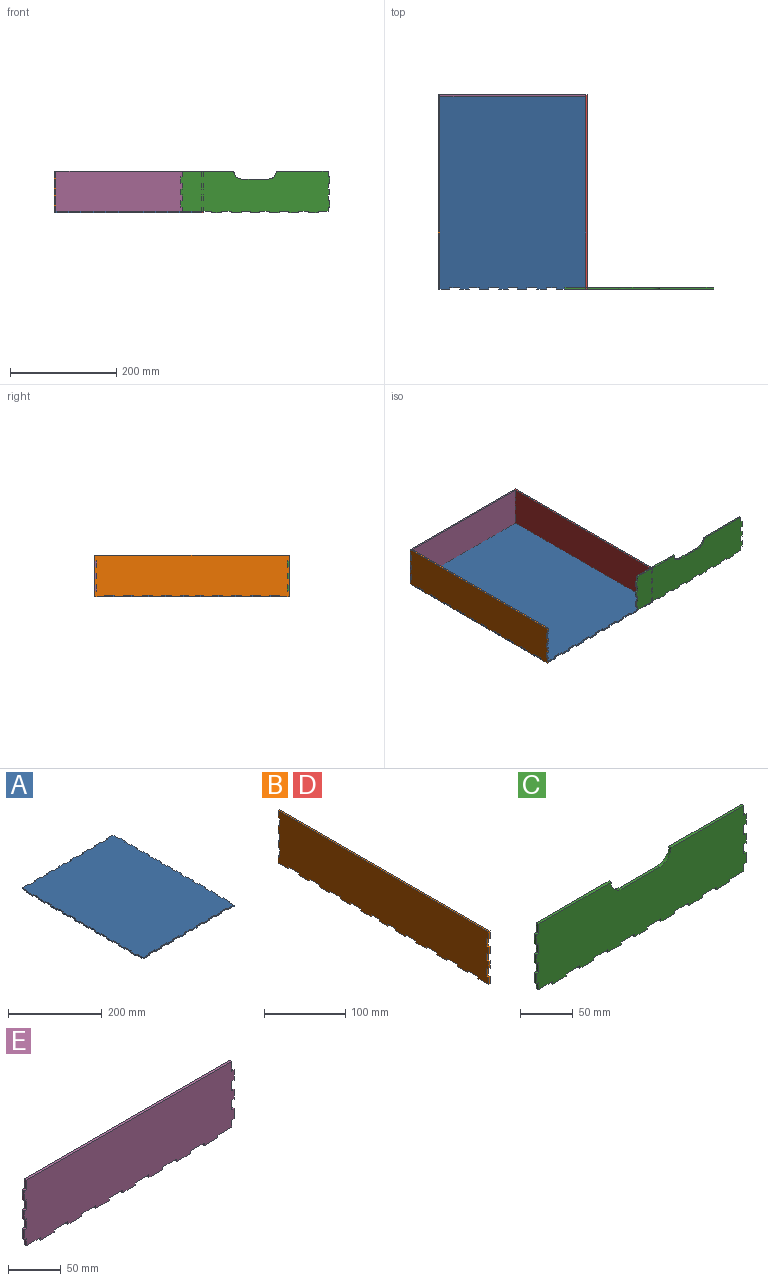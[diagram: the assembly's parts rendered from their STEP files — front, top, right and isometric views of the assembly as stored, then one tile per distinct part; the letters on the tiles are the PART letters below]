
ASSEMBLY  parts=5 mates=4
PART A: 142 faces, bbox 281x366x3 mm
  f0: plane 18x3mm, normal (-1,0,0), area 54mm2, adj f1,f139,f140,f141
  f1: plane 3x3mm, normal (0,1,0), area 9mm2, adj f0,f2,f140,f141
  f2: plane 18x3mm, normal (-1,0,0), area 54mm2, adj f1,f3,f140,f141
  f3: plane 3x3mm, normal (0,-1,0), area 9mm2, adj f2,f4,f140,f141
  f4: plane 18x3mm, normal (-1,0,0), area 54mm2, adj f3,f5,f140,f141
  f5: plane 3x3mm, normal (0,1,0), area 9mm2, adj f4,f6,f140,f141
  f6: plane 18x3mm, normal (-1,0,0), area 54mm2, adj f5,f7,f140,f141
  f7: plane 3x3mm, normal (0,-1,0), area 9mm2, adj f6,f8,f140,f141
  f8: plane 18x3mm, normal (-1,0,0), area 54mm2, adj f7,f9,f140,f141
  f9: plane 3x3mm, normal (0,1,0), area 9mm2, adj f8,f10,f140,f141
  f10: plane 18x3mm, normal (-1,0,0), area 54mm2, adj f9,f11,f140,f141
  f11: plane 3x3mm, normal (0,-1,0), area 9mm2, adj f10,f12,f140,f141
  f12: plane 18x3mm, normal (-1,0,0), area 54mm2, adj f11,f13,f140,f141
  f13: plane 3x3mm, normal (0,1,0), area 9mm2, adj f12,f14,f140,f141
  f14: plane 18x3mm, normal (-1,0,0), area 54mm2, adj f13,f15,f140,f141
  f15: plane 3x3mm, normal (0,-1,0), area 9mm2, adj f14,f16,f140,f141
  f16: plane 18x3mm, normal (-1,0,0), area 54mm2, adj f15,f17,f140,f141
  f17: plane 3x3mm, normal (0,1,0), area 9mm2, adj f16,f18,f140,f141
  f18: plane 14x3mm, normal (-1,0,0), area 42mm2, adj f17,f19,f140,f141
  f19: plane 3x3mm, normal (0,-1,0), area 9mm2, adj f18,f20,f140,f141
  f20: plane 14x3mm, normal (-1,0,0), area 42mm2, adj f19,f21,f140,f141
  f21: plane 3x3mm, normal (0,1,0), area 9mm2, adj f20,f22,f140,f141
  f22: plane 14x3mm, normal (-1,0,0), area 42mm2, adj f21,f23,f140,f141
  f23: plane 3x3mm, normal (0,-1,0), area 9mm2, adj f22,f24,f140,f141
  f24: plane 18x3mm, normal (-1,0,0), area 54mm2, adj f23,f25,f140,f141
  f25: plane 3x3mm, normal (0,1,0), area 9mm2, adj f24,f26,f140,f141
  f26: plane 18x3mm, normal (-1,0,0), area 54mm2, adj f25,f27,f140,f141
  f27: plane 3x3mm, normal (0,-1,0), area 9mm2, adj f26,f28,f140,f141
  f28: plane 18x3mm, normal (-1,0,0), area 54mm2, adj f27,f29,f140,f141
  f29: plane 3x3mm, normal (0,1,0), area 9mm2, adj f28,f30,f140,f141
  f30: plane 18x3mm, normal (-1,0,0), area 54mm2, adj f29,f31,f140,f141
  f31: plane 3x3mm, normal (0,-1,0), area 9mm2, adj f30,f32,f140,f141
  f32: plane 18x3mm, normal (-1,0,0), area 54mm2, adj f31,f33,f140,f141
  f33: plane 3x3mm, normal (0,1,0), area 9mm2, adj f32,f34,f140,f141
  f34: plane 18x3mm, normal (-1,0,0), area 54mm2, adj f33,f35,f140,f141
  f35: plane 3x3mm, normal (0,-1,0), area 9mm2, adj f34,f36,f140,f141
  f36: plane 18x3mm, normal (-1,0,0), area 54mm2, adj f35,f37,f140,f141
  f37: plane 3x3mm, normal (0,1,0), area 9mm2, adj f36,f38,f140,f141
  f38: plane 18x3mm, normal (-1,0,0), area 54mm2, adj f37,f39,f140,f141
  f39: plane 3x3mm, normal (0,-1,0), area 9mm2, adj f38,f40,f140,f141
  f40: plane 18x3mm, normal (-1,0,0), area 54mm2, adj f39,f41,f140,f141
  f41: plane 18.5x3mm, normal (0,-1,0), area 55.5mm2, adj f40,f42,f140,f141
  f42: plane 3x3mm, normal (1,0,0), area 9mm2, adj f41,f43,f140,f141
  f43: plane 18.5x3mm, normal (0,-1,0), area 55.5mm2, adj f42,f44,f140,f141
  f44: plane 3x3mm, normal (-1,0,0), area 9mm2, adj f43,f45,f140,f141
  f45: plane 18.5x3mm, normal (0,-1,0), area 55.5mm2, adj f44,f46,f140,f141
  f46: plane 3x3mm, normal (1,0,0), area 9mm2, adj f45,f47,f140,f141
  f47: plane 18.5x3mm, normal (0,-1,0), area 55.5mm2, adj f46,f48,f140,f141
  f48: plane 3x3mm, normal (-1,0,0), area 9mm2, adj f47,f49,f140,f141
  f49: plane 18.5x3mm, normal (0,-1,0), area 55.5mm2, adj f48,f50,f140,f141
  f50: plane 3x3mm, normal (1,0,0), area 9mm2, adj f49,f51,f140,f141
  f51: plane 18.5x3mm, normal (0,-1,0), area 55.5mm2, adj f50,f52,f140,f141
  f52: plane 3x3mm, normal (-1,0,0), area 9mm2, adj f51,f53,f140,f141
  f53: plane 18x3mm, normal (0,-1,0), area 54mm2, adj f52,f54,f140,f141
  f54: plane 3x3mm, normal (1,0,0), area 9mm2, adj f53,f55,f140,f141
  f55: plane 17x3mm, normal (0,-1,0), area 51mm2, adj f54,f56,f140,f141
  f56: plane 3x3mm, normal (-1,0,0), area 9mm2, adj f55,f57,f140,f141
  f57: plane 18x3mm, normal (0,-1,0), area 54mm2, adj f56,f58,f140,f141
  f58: plane 3x3mm, normal (1,0,0), area 9mm2, adj f57,f59,f140,f141
  f59: plane 18.5x3mm, normal (0,-1,0), area 55.5mm2, adj f58,f60,f140,f141
  f60: plane 3x3mm, normal (-1,0,0), area 9mm2, adj f59,f61,f140,f141
  f61: plane 18.5x3mm, normal (0,-1,0), area 55.5mm2, adj f60,f62,f140,f141
  f62: plane 3x3mm, normal (1,0,0), area 9mm2, adj f61,f63,f140,f141
  f63: plane 18.5x3mm, normal (0,-1,0), area 55.5mm2, adj f62,f64,f140,f141
  f64: plane 3x3mm, normal (-1,0,0), area 9mm2, adj f63,f65,f140,f141
  f65: plane 18.5x3mm, normal (0,-1,0), area 55.5mm2, adj f64,f66,f140,f141
  f66: plane 3x3mm, normal (1,0,0), area 9mm2, adj f65,f67,f140,f141
  f67: plane 18.5x3mm, normal (0,-1,0), area 55.5mm2, adj f66,f68,f140,f141
  f68: plane 3x3mm, normal (-1,0,0), area 9mm2, adj f67,f69,f140,f141
  f69: plane 18.5x3mm, normal (0,-1,0), area 55.5mm2, adj f68,f70,f140,f141
  f70: plane 18x3mm, normal (1,0,0), area 54mm2, adj f69,f71,f140,f141
  f71: plane 3x3mm, normal (0,-1,0), area 9mm2, adj f70,f72,f140,f141
  f72: plane 18x3mm, normal (1,0,0), area 54mm2, adj f71,f73,f140,f141
  f73: plane 3x3mm, normal (0,1,0), area 9mm2, adj f72,f74,f140,f141
  f74: plane 18x3mm, normal (1,0,0), area 54mm2, adj f73,f75,f140,f141
  f75: plane 3x3mm, normal (0,-1,0), area 9mm2, adj f74,f76,f140,f141
  f76: plane 18x3mm, normal (1,0,0), area 54mm2, adj f75,f77,f140,f141
  f77: plane 3x3mm, normal (0,1,0), area 9mm2, adj f76,f78,f140,f141
  f78: plane 18x3mm, normal (1,0,0), area 54mm2, adj f77,f79,f140,f141
  f79: plane 3x3mm, normal (0,-1,0), area 9mm2, adj f78,f80,f140,f141
  f80: plane 18x3mm, normal (1,0,0), area 54mm2, adj f79,f81,f140,f141
  f81: plane 3x3mm, normal (0,1,0), area 9mm2, adj f80,f82,f140,f141
  f82: plane 18x3mm, normal (1,0,0), area 54mm2, adj f81,f83,f140,f141
  f83: plane 3x3mm, normal (0,-1,0), area 9mm2, adj f82,f84,f140,f141
  f84: plane 18x3mm, normal (1,0,0), area 54mm2, adj f83,f85,f140,f141
  f85: plane 3x3mm, normal (0,1,0), area 9mm2, adj f84,f86,f140,f141
  f86: plane 18x3mm, normal (1,0,0), area 54mm2, adj f85,f87,f140,f141
  f87: plane 3x3mm, normal (0,-1,0), area 9mm2, adj f86,f88,f140,f141
  f88: plane 14x3mm, normal (1,0,0), area 42mm2, adj f87,f89,f140,f141
  f89: plane 3x3mm, normal (0,1,0), area 9mm2, adj f88,f90,f140,f141
  f90: plane 14x3mm, normal (1,0,0), area 42mm2, adj f89,f91,f140,f141
  f91: plane 3x3mm, normal (0,-1,0), area 9mm2, adj f90,f92,f140,f141
  f92: plane 14x3mm, normal (1,0,0), area 42mm2, adj f91,f93,f140,f141
  f93: plane 3x3mm, normal (0,1,0), area 9mm2, adj f92,f94,f140,f141
  f94: plane 18x3mm, normal (1,0,0), area 54mm2, adj f93,f95,f140,f141
  f95: plane 3x3mm, normal (0,-1,0), area 9mm2, adj f94,f96,f140,f141
  f96: plane 18x3mm, normal (1,0,0), area 54mm2, adj f95,f97,f140,f141
  f97: plane 3x3mm, normal (0,1,0), area 9mm2, adj f96,f98,f140,f141
  f98: plane 18x3mm, normal (1,0,0), area 54mm2, adj f97,f99,f140,f141
  f99: plane 3x3mm, normal (0,-1,0), area 9mm2, adj f98,f100,f140,f141
  f100: plane 18x3mm, normal (1,0,0), area 54mm2, adj f99,f101,f140,f141
  f101: plane 3x3mm, normal (0,1,0), area 9mm2, adj f100,f102,f140,f141
  f102: plane 18x3mm, normal (1,0,0), area 54mm2, adj f101,f103,f140,f141
  f103: plane 3x3mm, normal (0,-1,0), area 9mm2, adj f102,f104,f140,f141
  f104: plane 18x3mm, normal (1,0,0), area 54mm2, adj f103,f105,f140,f141
  f105: plane 3x3mm, normal (0,1,0), area 9mm2, adj f104,f106,f140,f141
  f106: plane 18x3mm, normal (1,0,0), area 54mm2, adj f105,f107,f140,f141
  f107: plane 3x3mm, normal (0,-1,0), area 9mm2, adj f106,f108,f140,f141
  f108: plane 18x3mm, normal (1,0,0), area 54mm2, adj f107,f109,f140,f141
  f109: plane 3x3mm, normal (0,1,0), area 9mm2, adj f108,f110,f140,f141
  f110: plane 18x3mm, normal (1,0,0), area 54mm2, adj f109,f111,f140,f141
  f111: plane 18.5x3mm, normal (0,1,0), area 55.5mm2, adj f110,f112,f140,f141
  f112: plane 3x3mm, normal (-1,0,0), area 9mm2, adj f111,f113,f140,f141
  f113: plane 18.5x3mm, normal (0,1,0), area 55.5mm2, adj f112,f114,f140,f141
  f114: plane 3x3mm, normal (1,0,0), area 9mm2, adj f113,f115,f140,f141
  f115: plane 18.5x3mm, normal (0,1,0), area 55.5mm2, adj f114,f116,f140,f141
  f116: plane 3x3mm, normal (-1,0,0), area 9mm2, adj f115,f117,f140,f141
  f117: plane 18.5x3mm, normal (0,1,0), area 55.5mm2, adj f116,f118,f140,f141
  f118: plane 3x3mm, normal (1,0,0), area 9mm2, adj f117,f119,f140,f141
  f119: plane 18.5x3mm, normal (0,1,0), area 55.5mm2, adj f118,f120,f140,f141
  f120: plane 3x3mm, normal (-1,0,0), area 9mm2, adj f119,f121,f140,f141
  f121: plane 18.5x3mm, normal (0,1,0), area 55.5mm2, adj f120,f122,f140,f141
  f122: plane 3x3mm, normal (1,0,0), area 9mm2, adj f121,f123,f140,f141
  f123: plane 18x3mm, normal (0,1,0), area 54mm2, adj f122,f124,f140,f141
  f124: plane 3x3mm, normal (-1,0,0), area 9mm2, adj f123,f125,f140,f141
  f125: plane 17x3mm, normal (0,1,0), area 51mm2, adj f124,f126,f140,f141
  f126: plane 3x3mm, normal (1,0,0), area 9mm2, adj f125,f127,f140,f141
  f127: plane 18x3mm, normal (0,1,0), area 54mm2, adj f126,f128,f140,f141
  f128: plane 3x3mm, normal (-1,0,0), area 9mm2, adj f127,f129,f140,f141
  f129: plane 18.5x3mm, normal (0,1,0), area 55.5mm2, adj f128,f130,f140,f141
  f130: plane 3x3mm, normal (1,0,0), area 9mm2, adj f129,f131,f140,f141
  f131: plane 18.5x3mm, normal (0,1,0), area 55.5mm2, adj f130,f132,f140,f141
  f132: plane 3x3mm, normal (-1,0,0), area 9mm2, adj f131,f133,f140,f141
  f133: plane 18.5x3mm, normal (0,1,0), area 55.5mm2, adj f132,f134,f140,f141
  f134: plane 3x3mm, normal (1,0,0), area 9mm2, adj f133,f135,f140,f141
  f135: plane 18.5x3mm, normal (0,1,0), area 55.5mm2, adj f134,f136,f140,f141
  f136: plane 3x3mm, normal (-1,0,0), area 9mm2, adj f135,f137,f140,f141
  f137: plane 18.5x3mm, normal (0,1,0), area 55.5mm2, adj f136,f138,f140,f141
  f138: plane 3x3mm, normal (1,0,0), area 9mm2, adj f137,f139,f140,f141
  f139: plane 18.5x3mm, normal (0,1,0), area 55.5mm2, adj f0,f138,f140,f141
  f140: plane 366x281mm, normal (0,0,1), area 100914mm2, adj f0,f1,f2,f3,f4,f5,f6,f7
  f141: plane 366x281mm, normal (0,0,-1), area 100914mm2, adj f0,f1,f2,f3,f4,f5,f6,f7
PART B: 70 faces, bbox 3x366x79 mm
  f0: plane 3x3mm, normal (0,-1,0), area 9mm2, adj f1,f67,f68,f69
  f1: plane 18x3mm, normal (0,0,-1), area 54mm2, adj f0,f2,f68,f69
  f2: plane 3x3mm, normal (0,1,0), area 9mm2, adj f1,f3,f68,f69
  f3: plane 18x3mm, normal (0,0,-1), area 54mm2, adj f2,f4,f68,f69
  f4: plane 3x3mm, normal (0,-1,0), area 9mm2, adj f3,f5,f68,f69
  f5: plane 18x3mm, normal (0,0,-1), area 54mm2, adj f4,f6,f68,f69
  f6: plane 3x3mm, normal (0,1,0), area 9mm2, adj f5,f7,f68,f69
  f7: plane 18x3mm, normal (0,0,-1), area 54mm2, adj f6,f8,f68,f69
  f8: plane 3x3mm, normal (0,-1,0), area 9mm2, adj f7,f9,f68,f69
  f9: plane 18x3mm, normal (0,0,-1), area 54mm2, adj f8,f10,f68,f69
  f10: plane 3x3mm, normal (0,1,0), area 9mm2, adj f9,f11,f68,f69
  f11: plane 14x3mm, normal (0,0,-1), area 42mm2, adj f10,f12,f68,f69
  f12: plane 3x3mm, normal (0,-1,0), area 9mm2, adj f11,f13,f68,f69
  f13: plane 14x3mm, normal (0,0,-1), area 42mm2, adj f12,f14,f68,f69
  f14: plane 3x3mm, normal (0,1,0), area 9mm2, adj f13,f15,f68,f69
  f15: plane 14x3mm, normal (0,0,-1), area 42mm2, adj f14,f16,f68,f69
  f16: plane 3x3mm, normal (0,-1,0), area 9mm2, adj f15,f17,f68,f69
  f17: plane 18x3mm, normal (0,0,-1), area 54mm2, adj f16,f18,f68,f69
  f18: plane 3x3mm, normal (0,1,0), area 9mm2, adj f17,f19,f68,f69
  f19: plane 18x3mm, normal (0,0,-1), area 54mm2, adj f18,f20,f68,f69
  f20: plane 3x3mm, normal (0,-1,0), area 9mm2, adj f19,f21,f68,f69
  f21: plane 18x3mm, normal (0,0,-1), area 54mm2, adj f20,f22,f68,f69
  f22: plane 3x3mm, normal (0,1,0), area 9mm2, adj f21,f23,f68,f69
  f23: plane 18x3mm, normal (0,0,-1), area 54mm2, adj f22,f24,f68,f69
  f24: plane 3x3mm, normal (0,-1,0), area 9mm2, adj f23,f25,f68,f69
  f25: plane 18x3mm, normal (0,0,-1), area 54mm2, adj f24,f26,f68,f69
  f26: plane 3x3mm, normal (0,1,0), area 9mm2, adj f25,f27,f68,f69
  f27: plane 18x3mm, normal (0,0,-1), area 54mm2, adj f26,f28,f68,f69
  f28: plane 3x3mm, normal (0,-1,0), area 9mm2, adj f27,f29,f68,f69
  f29: plane 18x3mm, normal (0,0,-1), area 54mm2, adj f28,f30,f68,f69
  f30: plane 3x3mm, normal (0,1,0), area 9mm2, adj f29,f31,f68,f69
  f31: plane 18x3mm, normal (0,0,-1), area 54mm2, adj f30,f32,f68,f69
  f32: plane 3x3mm, normal (0,-1,0), area 9mm2, adj f31,f33,f68,f69
  f33: plane 18x3mm, normal (0,0,-1), area 54mm2, adj f32,f34,f68,f69
  f34: plane 11x3mm, normal (0,1,0), area 33mm2, adj f33,f35,f68,f69
  f35: plane 3x3mm, normal (0,0,1), area 9mm2, adj f34,f36,f68,f69
  f36: plane 12x3mm, normal (0,1,0), area 36mm2, adj f35,f37,f68,f69
  f37: plane 3x3mm, normal (0,0,-1), area 9mm2, adj f36,f38,f68,f69
  f38: plane 11x3mm, normal (0,1,0), area 33mm2, adj f37,f39,f68,f69
  f39: plane 3x3mm, normal (0,0,1), area 9mm2, adj f38,f40,f68,f69
  f40: plane 11x3mm, normal (0,1,0), area 33mm2, adj f39,f41,f68,f69
  f41: plane 3x3mm, normal (0,0,-1), area 9mm2, adj f40,f42,f68,f69
  f42: plane 11x3mm, normal (0,1,0), area 33mm2, adj f41,f43,f68,f69
  f43: plane 3x3mm, normal (0,0,1), area 9mm2, adj f42,f44,f68,f69
  f44: plane 12x3mm, normal (0,1,0), area 36mm2, adj f43,f45,f68,f69
  f45: plane 3x3mm, normal (0,0,-1), area 9mm2, adj f44,f46,f68,f69
  f46: plane 11x3mm, normal (0,1,0), area 33mm2, adj f45,f47,f68,f69
  f47: plane 366x3mm, normal (0,0,1), area 1098mm2, adj f46,f48,f68,f69
  f48: plane 11x3mm, normal (0,-1,0), area 33mm2, adj f47,f49,f68,f69
  f49: plane 3x3mm, normal (0,0,-1), area 9mm2, adj f48,f50,f68,f69
  f50: plane 12x3mm, normal (0,-1,0), area 36mm2, adj f49,f51,f68,f69
  f51: plane 3x3mm, normal (0,0,1), area 9mm2, adj f50,f52,f68,f69
  f52: plane 11x3mm, normal (0,-1,0), area 33mm2, adj f51,f53,f68,f69
  f53: plane 3x3mm, normal (0,0,-1), area 9mm2, adj f52,f54,f68,f69
  f54: plane 11x3mm, normal (0,-1,0), area 33mm2, adj f53,f55,f68,f69
  f55: plane 3x3mm, normal (0,0,1), area 9mm2, adj f54,f56,f68,f69
  f56: plane 11x3mm, normal (0,-1,0), area 33mm2, adj f55,f57,f68,f69
  f57: plane 3x3mm, normal (0,0,-1), area 9mm2, adj f56,f58,f68,f69
  f58: plane 12x3mm, normal (0,-1,0), area 36mm2, adj f57,f59,f68,f69
  f59: plane 3x3mm, normal (0,0,1), area 9mm2, adj f58,f60,f68,f69
  f60: plane 11x3mm, normal (0,-1,0), area 33mm2, adj f59,f61,f68,f69
  f61: plane 18x3mm, normal (0,0,-1), area 54mm2, adj f60,f62,f68,f69
  f62: plane 3x3mm, normal (0,1,0), area 9mm2, adj f61,f63,f68,f69
  f63: plane 18x3mm, normal (0,0,-1), area 54mm2, adj f62,f64,f68,f69
  f64: plane 3x3mm, normal (0,-1,0), area 9mm2, adj f63,f65,f68,f69
  f65: plane 18x3mm, normal (0,0,-1), area 54mm2, adj f64,f66,f68,f69
  f66: plane 3x3mm, normal (0,1,0), area 9mm2, adj f65,f67,f68,f69
  f67: plane 18x3mm, normal (0,0,-1), area 54mm2, adj f0,f66,f68,f69
  f68: plane 366x79mm, normal (1,0,0), area 28188mm2, adj f0,f1,f2,f3,f4,f5,f6,f7
  f69: plane 366x79mm, normal (-1,0,0), area 28188mm2, adj f0,f1,f2,f3,f4,f5,f6,f7
PART C: 62 faces, bbox 281x3x79 mm
  f0: plane 3x3mm, normal (0,0,-1), area 9mm2, adj f1,f59,f60,f61
  f1: plane 11x3mm, normal (1,0,0), area 33mm2, adj f0,f2,f60,f61
  f2: plane 3x3mm, normal (0,0,1), area 9mm2, adj f1,f3,f60,f61
  f3: plane 11x3mm, normal (1,0,0), area 33mm2, adj f2,f4,f60,f61
  f4: plane 3x3mm, normal (0,0,-1), area 9mm2, adj f3,f5,f60,f61
  f5: plane 12x3mm, normal (1,0,0), area 36mm2, adj f4,f6,f60,f61
  f6: plane 3x3mm, normal (0,0,1), area 9mm2, adj f5,f7,f60,f61
  f7: plane 11x3mm, normal (1,0,0), area 33mm2, adj f6,f8,f60,f61
  f8: plane 97.5x3mm, normal (0,0,1), area 292.5mm2, adj f7,f9,f60,f61
  f9: cylinder r=15mm len=15mm, axis (0,-1,0), area 70.7mm2, adj f8,f10,f60,f61
  f10: plane 50x3mm, normal (0,0,1), area 150mm2, adj f9,f11,f60,f61
  f11: cylinder r=15mm len=15mm, axis (0,-1,0), area 70.7mm2, adj f10,f12,f60,f61
  f12: plane 97.5x3mm, normal (0,0,1), area 292.5mm2, adj f11,f13,f60,f61
  f13: plane 11x3mm, normal (-1,0,0), area 33mm2, adj f12,f14,f60,f61
  f14: plane 3x3mm, normal (0,0,1), area 9mm2, adj f13,f15,f60,f61
  f15: plane 12x3mm, normal (-1,0,0), area 36mm2, adj f14,f16,f60,f61
  f16: plane 3x3mm, normal (0,0,-1), area 9mm2, adj f15,f17,f60,f61
  f17: plane 11x3mm, normal (-1,0,0), area 33mm2, adj f16,f18,f60,f61
  f18: plane 3x3mm, normal (0,0,1), area 9mm2, adj f17,f19,f60,f61
  f19: plane 11x3mm, normal (-1,0,0), area 33mm2, adj f18,f20,f60,f61
  f20: plane 3x3mm, normal (0,0,-1), area 9mm2, adj f19,f21,f60,f61
  f21: plane 11x3mm, normal (-1,0,0), area 33mm2, adj f20,f22,f60,f61
  f22: plane 3x3mm, normal (0,0,1), area 9mm2, adj f21,f23,f60,f61
  f23: plane 12x3mm, normal (-1,0,0), area 36mm2, adj f22,f24,f60,f61
  f24: plane 3x3mm, normal (0,0,-1), area 9mm2, adj f23,f25,f60,f61
  f25: plane 8x3mm, normal (-1,0,0), area 24mm2, adj f24,f26,f60,f61
  f26: plane 18.5x3mm, normal (0,0,-1), area 55.5mm2, adj f25,f27,f60,f61
  f27: plane 3x3mm, normal (-1,0,0), area 9mm2, adj f26,f28,f60,f61
  f28: plane 18.5x3mm, normal (0,0,-1), area 55.5mm2, adj f27,f29,f60,f61
  f29: plane 3x3mm, normal (1,0,0), area 9mm2, adj f28,f30,f60,f61
  f30: plane 18.5x3mm, normal (0,0,-1), area 55.5mm2, adj f29,f31,f60,f61
  f31: plane 3x3mm, normal (-1,0,0), area 9mm2, adj f30,f32,f60,f61
  f32: plane 18.5x3mm, normal (0,0,-1), area 55.5mm2, adj f31,f33,f60,f61
  f33: plane 3x3mm, normal (1,0,0), area 9mm2, adj f32,f34,f60,f61
  f34: plane 18.5x3mm, normal (0,0,-1), area 55.5mm2, adj f33,f35,f60,f61
  f35: plane 3x3mm, normal (-1,0,0), area 9mm2, adj f34,f36,f60,f61
  f36: plane 18.5x3mm, normal (0,0,-1), area 55.5mm2, adj f35,f37,f60,f61
  f37: plane 3x3mm, normal (1,0,0), area 9mm2, adj f36,f38,f60,f61
  f38: plane 18x3mm, normal (0,0,-1), area 54mm2, adj f37,f39,f60,f61
  f39: plane 3x3mm, normal (-1,0,0), area 9mm2, adj f38,f40,f60,f61
  f40: plane 17x3mm, normal (0,0,-1), area 51mm2, adj f39,f41,f60,f61
  f41: plane 3x3mm, normal (1,0,0), area 9mm2, adj f40,f42,f60,f61
  f42: plane 18x3mm, normal (0,0,-1), area 54mm2, adj f41,f43,f60,f61
  f43: plane 3x3mm, normal (-1,0,0), area 9mm2, adj f42,f44,f60,f61
  f44: plane 18.5x3mm, normal (0,0,-1), area 55.5mm2, adj f43,f45,f60,f61
  f45: plane 3x3mm, normal (1,0,0), area 9mm2, adj f44,f46,f60,f61
  f46: plane 18.5x3mm, normal (0,0,-1), area 55.5mm2, adj f45,f47,f60,f61
  f47: plane 3x3mm, normal (-1,0,0), area 9mm2, adj f46,f48,f60,f61
  f48: plane 18.5x3mm, normal (0,0,-1), area 55.5mm2, adj f47,f49,f60,f61
  f49: plane 3x3mm, normal (1,0,0), area 9mm2, adj f48,f50,f60,f61
  f50: plane 18.5x3mm, normal (0,0,-1), area 55.5mm2, adj f49,f51,f60,f61
  f51: plane 3x3mm, normal (-1,0,0), area 9mm2, adj f50,f52,f60,f61
  f52: plane 18.5x3mm, normal (0,0,-1), area 55.5mm2, adj f51,f53,f60,f61
  f53: plane 3x3mm, normal (1,0,0), area 9mm2, adj f52,f54,f60,f61
  f54: plane 18.5x3mm, normal (0,0,-1), area 55.5mm2, adj f53,f55,f60,f61
  f55: plane 8x3mm, normal (1,0,0), area 24mm2, adj f54,f56,f60,f61
  f56: plane 3x3mm, normal (0,0,-1), area 9mm2, adj f55,f57,f60,f61
  f57: plane 12x3mm, normal (1,0,0), area 36mm2, adj f56,f58,f60,f61
  f58: plane 3x3mm, normal (0,0,1), area 9mm2, adj f57,f59,f60,f61
  f59: plane 11x3mm, normal (1,0,0), area 33mm2, adj f0,f58,f60,f61
  f60: plane 281x79mm, normal (0,-1,0), area 20390.6mm2, adj f0,f1,f2,f3,f4,f5,f6,f7
  f61: plane 281x79mm, normal (0,1,0), area 20390.6mm2, adj f0,f1,f2,f3,f4,f5,f6,f7
PART D: same geometry as B
PART E: 58 faces, bbox 281x3x79 mm
  f0: plane 3x3mm, normal (0,0,1), area 9mm2, adj f1,f55,f56,f57
  f1: plane 11x3mm, normal (1,0,0), area 33mm2, adj f0,f2,f56,f57
  f2: plane 3x3mm, normal (0,0,-1), area 9mm2, adj f1,f3,f56,f57
  f3: plane 11x3mm, normal (1,0,0), area 33mm2, adj f2,f4,f56,f57
  f4: plane 3x3mm, normal (0,0,1), area 9mm2, adj f3,f5,f56,f57
  f5: plane 11x3mm, normal (1,0,0), area 33mm2, adj f4,f6,f56,f57
  f6: plane 3x3mm, normal (0,0,-1), area 9mm2, adj f5,f7,f56,f57
  f7: plane 12x3mm, normal (1,0,0), area 36mm2, adj f6,f8,f56,f57
  f8: plane 3x3mm, normal (0,0,1), area 9mm2, adj f7,f9,f56,f57
  f9: plane 11x3mm, normal (1,0,0), area 33mm2, adj f8,f10,f56,f57
  f10: plane 275x3mm, normal (0,0,1), area 825mm2, adj f9,f11,f56,f57
  f11: plane 11x3mm, normal (-1,0,0), area 33mm2, adj f10,f12,f56,f57
  f12: plane 3x3mm, normal (0,0,1), area 9mm2, adj f11,f13,f56,f57
  f13: plane 12x3mm, normal (-1,0,0), area 36mm2, adj f12,f14,f56,f57
  f14: plane 3x3mm, normal (0,0,-1), area 9mm2, adj f13,f15,f56,f57
  f15: plane 11x3mm, normal (-1,0,0), area 33mm2, adj f14,f16,f56,f57
  f16: plane 3x3mm, normal (0,0,1), area 9mm2, adj f15,f17,f56,f57
  f17: plane 11x3mm, normal (-1,0,0), area 33mm2, adj f16,f18,f56,f57
  f18: plane 3x3mm, normal (0,0,-1), area 9mm2, adj f17,f19,f56,f57
  f19: plane 11x3mm, normal (-1,0,0), area 33mm2, adj f18,f20,f56,f57
  f20: plane 3x3mm, normal (0,0,1), area 9mm2, adj f19,f21,f56,f57
  f21: plane 12x3mm, normal (-1,0,0), area 36mm2, adj f20,f22,f56,f57
  f22: plane 3x3mm, normal (0,0,-1), area 9mm2, adj f21,f23,f56,f57
  f23: plane 8x3mm, normal (-1,0,0), area 24mm2, adj f22,f24,f56,f57
  f24: plane 18.5x3mm, normal (0,0,-1), area 55.5mm2, adj f23,f25,f56,f57
  f25: plane 3x3mm, normal (-1,0,0), area 9mm2, adj f24,f26,f56,f57
  f26: plane 18.5x3mm, normal (0,0,-1), area 55.5mm2, adj f25,f27,f56,f57
  f27: plane 3x3mm, normal (1,0,0), area 9mm2, adj f26,f28,f56,f57
  f28: plane 18.5x3mm, normal (0,0,-1), area 55.5mm2, adj f27,f29,f56,f57
  f29: plane 3x3mm, normal (-1,0,0), area 9mm2, adj f28,f30,f56,f57
  f30: plane 18.5x3mm, normal (0,0,-1), area 55.5mm2, adj f29,f31,f56,f57
  f31: plane 3x3mm, normal (1,0,0), area 9mm2, adj f30,f32,f56,f57
  f32: plane 18.5x3mm, normal (0,0,-1), area 55.5mm2, adj f31,f33,f56,f57
  f33: plane 3x3mm, normal (-1,0,0), area 9mm2, adj f32,f34,f56,f57
  f34: plane 18.5x3mm, normal (0,0,-1), area 55.5mm2, adj f33,f35,f56,f57
  f35: plane 3x3mm, normal (1,0,0), area 9mm2, adj f34,f36,f56,f57
  f36: plane 18x3mm, normal (0,0,-1), area 54mm2, adj f35,f37,f56,f57
  f37: plane 3x3mm, normal (-1,0,0), area 9mm2, adj f36,f38,f56,f57
  f38: plane 17x3mm, normal (0,0,-1), area 51mm2, adj f37,f39,f56,f57
  f39: plane 3x3mm, normal (1,0,0), area 9mm2, adj f38,f40,f56,f57
  f40: plane 18x3mm, normal (0,0,-1), area 54mm2, adj f39,f41,f56,f57
  f41: plane 3x3mm, normal (-1,0,0), area 9mm2, adj f40,f42,f56,f57
  f42: plane 18.5x3mm, normal (0,0,-1), area 55.5mm2, adj f41,f43,f56,f57
  f43: plane 3x3mm, normal (1,0,0), area 9mm2, adj f42,f44,f56,f57
  f44: plane 18.5x3mm, normal (0,0,-1), area 55.5mm2, adj f43,f45,f56,f57
  f45: plane 3x3mm, normal (-1,0,0), area 9mm2, adj f44,f46,f56,f57
  f46: plane 18.5x3mm, normal (0,0,-1), area 55.5mm2, adj f45,f47,f56,f57
  f47: plane 3x3mm, normal (1,0,0), area 9mm2, adj f46,f48,f56,f57
  f48: plane 18.5x3mm, normal (0,0,-1), area 55.5mm2, adj f47,f49,f56,f57
  f49: plane 3x3mm, normal (-1,0,0), area 9mm2, adj f48,f50,f56,f57
  f50: plane 18.5x3mm, normal (0,0,-1), area 55.5mm2, adj f49,f51,f56,f57
  f51: plane 3x3mm, normal (1,0,0), area 9mm2, adj f50,f52,f56,f57
  f52: plane 18.5x3mm, normal (0,0,-1), area 55.5mm2, adj f51,f53,f56,f57
  f53: plane 8x3mm, normal (1,0,0), area 24mm2, adj f52,f54,f56,f57
  f54: plane 3x3mm, normal (0,0,-1), area 9mm2, adj f53,f55,f56,f57
  f55: plane 12x3mm, normal (1,0,0), area 36mm2, adj f0,f54,f56,f57
  f56: plane 281x79mm, normal (0,-1,0), area 21494mm2, adj f0,f1,f2,f3,f4,f5,f6,f7
  f57: plane 281x79mm, normal (0,1,0), area 21494mm2, adj f0,f1,f2,f3,f4,f5,f6,f7
PLACE A t=(14.22,6.45,-4.14)mm
PLACE B t=(-126.28,6.45,35.36)mm
PLACE C t=(252.22,-173.55,35.36)mm
PLACE D t=(151.72,6.45,35.36)mm
PLACE E t=(14.22,189.45,35.36)mm
MATE fastened C.f60 <-> A.f69  axis (0,-1,0) through (133.22,-176.55,-4.14)mm
MATE fastened B.f69 <-> A.f38  axis (-1,0,0) through (-126.28,-140.55,-1.14)mm
MATE fastened E.f57 <-> A.f111  axis (0,1,0) through (133.22,189.45,-1.14)mm
MATE fastened D.f68 <-> A.f72  axis (1,0,0) through (154.72,-140.55,-1.14)mm
